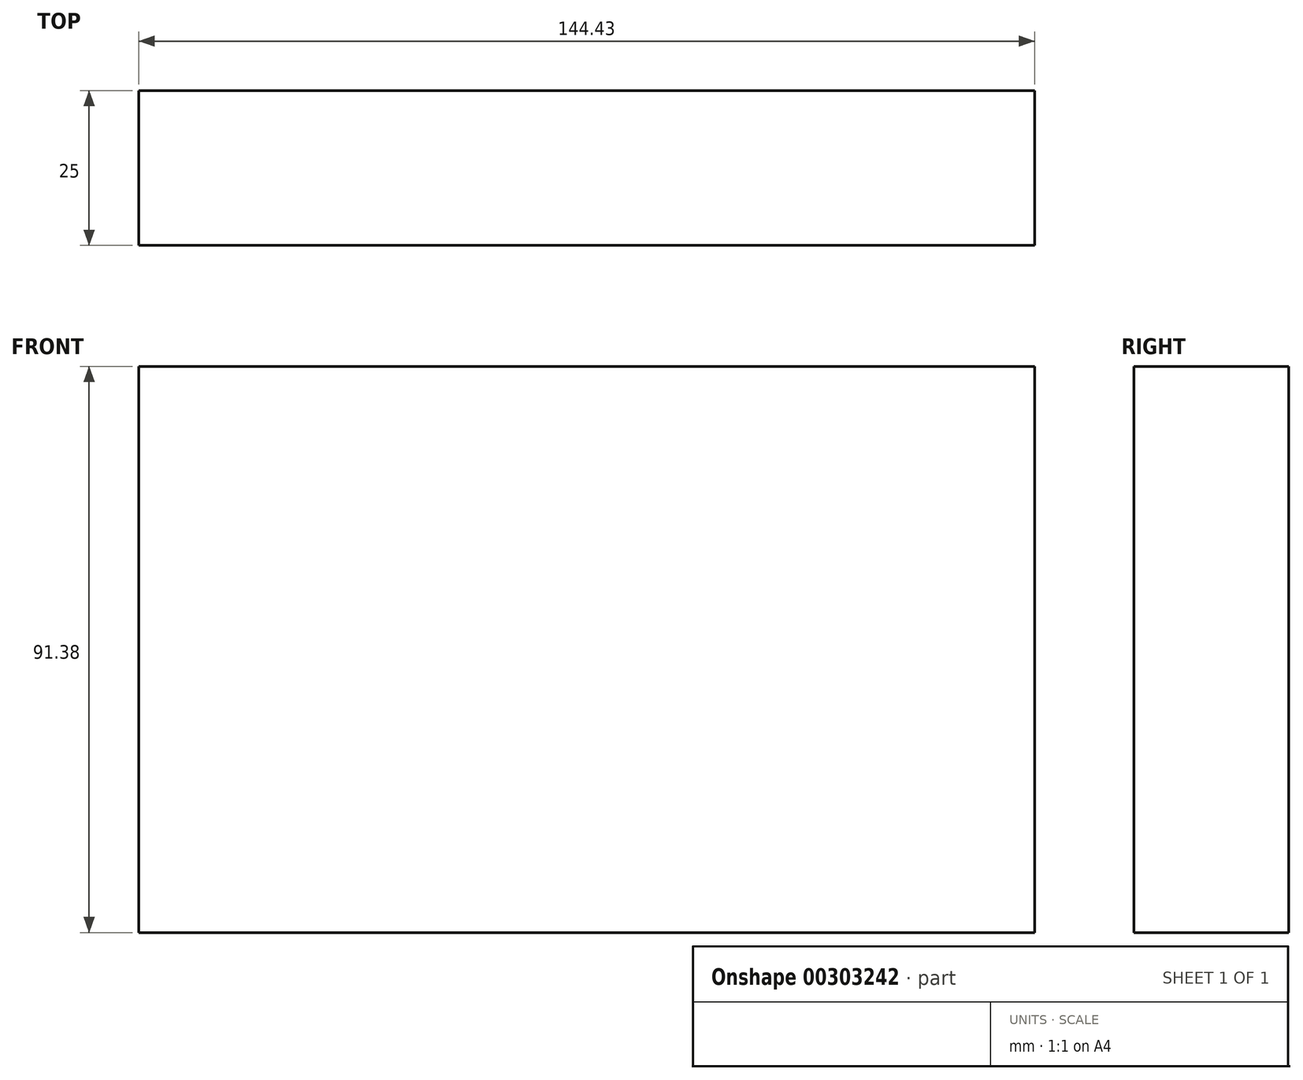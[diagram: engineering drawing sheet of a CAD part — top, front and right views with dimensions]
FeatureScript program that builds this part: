
annotation { "Feature Type Name" : "Feature", "Feature Type Description" : "" }
export const myFeature = defineFeature(function(context is Context, id is Id, definition is map)
    precondition{}
    {
        {
            var Q0;
            Q0=qCreatedBy(makeId("Front.planeOp"),FACE);
            var sketch = newSketch(context, id + "F0", { "sketchPlane" : qUnion([Q0])});
            skLineSegment(sketch, "E0.bottom", {"start": v(-68.16, 60.5) * mm, "end": v(76.27, 60.5) * mm});
            skLineSegment(sketch, "E0.top", {"start": v(-68.16, -30.89) * mm, "end": v(76.27, -30.89) * mm});
            skLineSegment(sketch, "E0.left", {"start": v(-68.16, 60.5) * mm, "end": v(-68.16, -30.89) * mm});
            skLineSegment(sketch, "E0.right", {"start": v(76.27, 60.5) * mm, "end": v(76.27, -30.89) * mm});
            skSolve(sketch);
        }
        {
            var Q0;
            Q0=makeQuery(id+"F0.imprint","IMPRINT",FACE,{"disambiguationData":[TD([[makeQuery(id+"F0.imprint","IMPRINT",EDGE,{"derivedFrom":sQuery(id+"F0.wireOp",EDGE,"E0.bottom")}),-1.0]])]});
            extrude(context, id + "F1", {"entities" : qUnion([Q0]), "depth" : 25 * mm});
        }
    });
